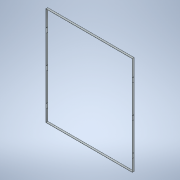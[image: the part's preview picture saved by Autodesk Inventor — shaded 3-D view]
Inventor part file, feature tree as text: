
AUTODESK INVENTOR PART (.ipt)
format: ipt  version: 2021 (Build 250183000, 183)  size: 174,080 bytes
history: native  units: mm
features: extrude x3, sketch x3, mirror x2, pattern_linear x1
ambient origin geometry x8: Origin, YZ Plane, XZ Plane, XY Plane, X Axis, Y Axis, Z Axis, Center Point
bodies: Solid1 (feature_tree)
feature tree (9):
  extrude  "Extrusion1"  Depth=2100.0mm
  extrude  "Extrusion2"  Depth=40.0mm TaperAngle=0.0deg
  mirror  "Mirror1"
  extrude  "Extrusion3"  Depth=700.0mm
  pattern_linear  "Rectangular Pattern1"  Spacing1=2.5mm  [1 undecoded]
  mirror  "Mirror2"
  sketch  "Sketch1"  dims[d0=1840.0mm d1=2100.0mm]
  sketch  "Sketch2"  dims[d2=4.0mm d3=40.0mm d4=0.0mm]
  sketch  "Sketch3"  dims[d5=100.0mm d7=30.0mm d9=700.0mm d10=10.0mm d12=10.0mm d14=2.5mm d15=0.0mm d16=8.0mm d17=20.0mm d18=10.0mm d19=1.0mm d20=0.0mm d21=30.0mm d23=700.0mm d24=350.0mm]
note: 1 required parameter value undecoded (feature->parameter linkage not recoverable at this tier; creation-order binding heuristic only, values carry confidence <= 0.55)
